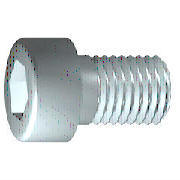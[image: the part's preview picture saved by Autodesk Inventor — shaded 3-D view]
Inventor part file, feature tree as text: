
AUTODESK INVENTOR PART (.ipt)
format: ipt  version: 2022 (Build 260153000, 153)  size: 193,024 bytes
history: native  units: mm (DEFAULTED — no unit token found)
features: sketch x2, other x1, extrude x1, plane x1, fillet x1
ambient origin geometry x7: Origin, YZ Plane, XY Plane, X Axis, Y Axis, Z Axis, Center Point
bodies: Solid1 (feature_tree)
feature tree (6):
  other  "Базовый элемент"
  extrude  "Паз"  Depth=8.65mm
  plane  "Work Plane1"
  fillet  "Fillet2"  Radius=0.276153mm
  sketch  "Эскиз1"
  sketch  "Эскиз2"
